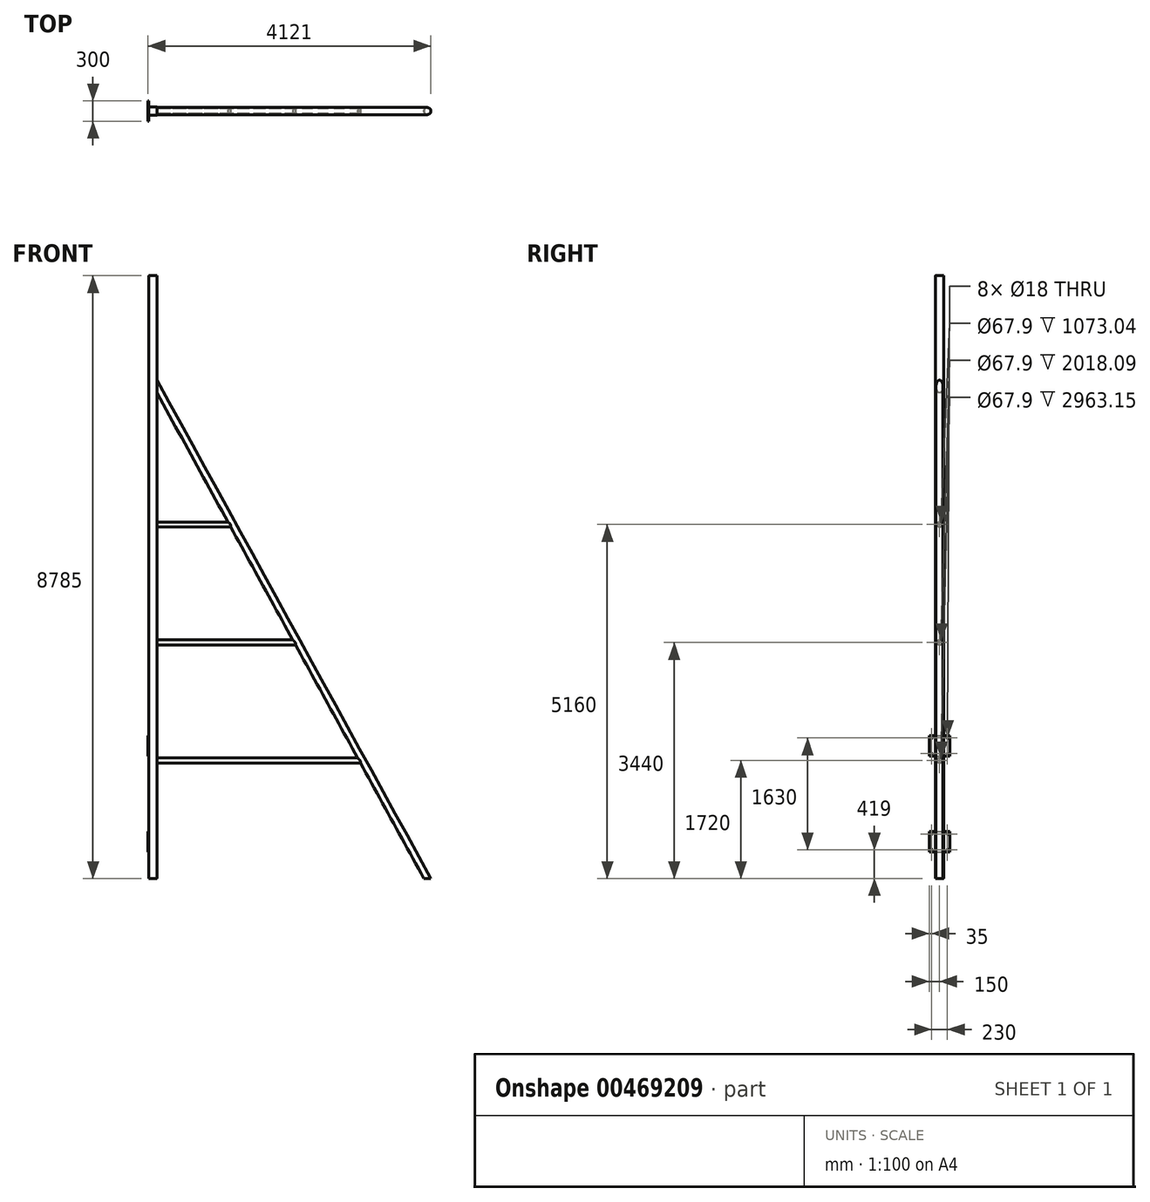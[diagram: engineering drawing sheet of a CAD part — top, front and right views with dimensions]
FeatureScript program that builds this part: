
annotation { "Feature Type Name" : "Feature", "Feature Type Description" : "" }
export const myFeature = defineFeature(function(context is Context, id is Id, definition is map)
    precondition{}
    {
        {
            var Q0;
            Q0=qCreatedBy(makeId("Top.planeOp"),FACE);
            var sketch = newSketch(context, id + "F0", { "sketchPlane" : qUnion([Q0])});
            skLineSegment(sketch, "E0.bottom", {"start": v(54, 60) * mm, "end": v(-54, 60) * mm});
            skLineSegment(sketch, "E0.top", {"start": v(54, -60) * mm, "end": v(-54, -60) * mm});
            skLineSegment(sketch, "E0.left", {"start": v(60, 54) * mm, "end": v(60, -54) * mm});
            skLineSegment(sketch, "E0.right", {"start": v(-60, 54) * mm, "end": v(-60, -54) * mm});
            skPoint(sketch, "E0.middle", {"position": v(0, 0) * mm});
            skLineSegment(sketch, "E1.0", {"start": v(51, 54) * mm, "end": v(-51, 54) * mm});
            skLineSegment(sketch, "E1.1", {"start": v(54, 51) * mm, "end": v(54, -51) * mm});
            skLineSegment(sketch, "E1.2", {"start": v(51, -54) * mm, "end": v(-51, -54) * mm});
            skLineSegment(sketch, "E1.3", {"start": v(-54, 51) * mm, "end": v(-54, -51) * mm});
            skPoint(sketch, "E2.visualSharp", {"position": v(-54, 54) * mm});
            skArc(sketch, "E2.filletArc", {"start": v(-51, 54) * mm, "mid": v(-53.12, 53.12) * mm, "end": v(-54, 51) * mm});
            skPoint(sketch, "E3.visualSharp", {"position": v(54, 54) * mm});
            skArc(sketch, "E3.filletArc", {"start": v(54, 51) * mm, "mid": v(53.12, 53.12) * mm, "end": v(51, 54) * mm});
            skPoint(sketch, "E4.visualSharp", {"position": v(54, -54) * mm});
            skArc(sketch, "E4.filletArc", {"start": v(51, -54) * mm, "mid": v(53.12, -53.12) * mm, "end": v(54, -51) * mm});
            skPoint(sketch, "E5.visualSharp", {"position": v(-54, -54) * mm});
            skArc(sketch, "E5.filletArc", {"start": v(-54, -51) * mm, "mid": v(-53.12, -53.12) * mm, "end": v(-51, -54) * mm});
            skPoint(sketch, "E6.visualSharp", {"position": v(60, -60) * mm});
            skArc(sketch, "E6.filletArc", {"start": v(54, -60) * mm, "mid": v(58.24, -58.24) * mm, "end": v(60, -54) * mm});
            skPoint(sketch, "E7.visualSharp", {"position": v(60, 60) * mm});
            skArc(sketch, "E7.filletArc", {"start": v(60, 54) * mm, "mid": v(58.24, 58.24) * mm, "end": v(54, 60) * mm});
            skPoint(sketch, "E8.visualSharp", {"position": v(-60, 60) * mm});
            skArc(sketch, "E8.filletArc", {"start": v(-54, 60) * mm, "mid": v(-58.24, 58.24) * mm, "end": v(-60, 54) * mm});
            skPoint(sketch, "E9.visualSharp", {"position": v(-60, -60) * mm});
            skArc(sketch, "E9.filletArc", {"start": v(-60, -54) * mm, "mid": v(-58.24, -58.24) * mm, "end": v(-54, -60) * mm});
            skSolve(sketch);
        }
        {
            var Q0;
            Q0=qSketchRegion(id+"F0",true);
            extrude(context, id + "F1", {"entities" : qUnion([Q0]), "depth" : 8780 * mm});
        }
        {
            var Q0;
            Q0=qCreatedBy(makeId("Top.planeOp"),FACE);
            var sketch = newSketch(context, id + "F2", { "sketchPlane" : qUnion([Q0])});
            skCircle(sketch, "E10", {"center": v(4000, 0) * mm, "radius": 48.15 * mm});
            skCircle(sketch, "E11", {"center": v(4000, 0) * mm, "radius": 51 * mm});
            skSolve(sketch);
        }
        {
            var Q0;
            Q0=qCreatedBy(makeId("Front.planeOp"),FACE);
            var sketch = newSketch(context, id + "F3", { "sketchPlane" : qUnion([Q0])});
            skLineSegment(sketch, "E12", {"start": v(4000, 0) * mm, "end": v(0, 7280) * mm});
            skSolve(sketch);
        }
        {
            var Q0;
            Q0=makeQuery(id+"F2.imprint","IMPRINT",FACE,{"disambiguationData":[TD([[makeQuery(id+"F2.imprint","IMPRINT",EDGE,{"derivedFrom":sQuery(id+"F2.wireOp",EDGE,"E10")}),-1.0]])]});
            var Q1;
            Q1=sQuery(id+"F3.wireOp",EDGE,"E12");
            sweep(context, id + "F4", {"operationType" : NewBodyOperationType.ADD, "profiles" : qUnion([Q0]), "path" : qUnion([Q1])});
        }
        {
            var Q0;
            Q0=makeQuery(id+"F1.opExtrude","CAP_FACE",FACE,{"disambiguationData":[OSD([sQuery(id+"F0.wireOp",EDGE,"E0.bottom"),sQuery(id+"F0.wireOp",EDGE,"E0.top"),sQuery(id+"F0.wireOp",EDGE,"E0.left"),sQuery(id+"F0.wireOp",EDGE,"E0.right"),sQuery(id+"F0.wireOp",EDGE,"E1.0"),sQuery(id+"F0.wireOp",EDGE,"E1.1"),sQuery(id+"F0.wireOp",EDGE,"E1.2"),sQuery(id+"F0.wireOp",EDGE,"E1.3"),sQuery(id+"F0.wireOp",EDGE,"E2.filletArc"),sQuery(id+"F0.wireOp",EDGE,"E3.filletArc"),sQuery(id+"F0.wireOp",EDGE,"E4.filletArc"),sQuery(id+"F0.wireOp",EDGE,"E5.filletArc"),sQuery(id+"F0.wireOp",EDGE,"E6.filletArc"),sQuery(id+"F0.wireOp",EDGE,"E7.filletArc"),sQuery(id+"F0.wireOp",EDGE,"E8.filletArc"),sQuery(id+"F0.wireOp",EDGE,"E9.filletArc")])],"isStart":false});
            var sketch = newSketch(context, id + "F5", { "sketchPlane" : qUnion([Q0])});
            skLineSegment(sketch, "E13.0", {"start": v(51, -54) * mm, "end": v(-51, -54) * mm});
            skArc(sketch, "E13.1", {"start": v(51, -54) * mm, "mid": v(53.12, -53.12) * mm, "end": v(54, -51) * mm});
            skLineSegment(sketch, "E13.2", {"start": v(54, 51) * mm, "end": v(54, -51) * mm});
            skArc(sketch, "E13.3", {"start": v(54, 51) * mm, "mid": v(53.12, 53.12) * mm, "end": v(51, 54) * mm});
            skLineSegment(sketch, "E13.4", {"start": v(51, 54) * mm, "end": v(-51, 54) * mm});
            skArc(sketch, "E13.5", {"start": v(-51, 54) * mm, "mid": v(-53.12, 53.12) * mm, "end": v(-54, 51) * mm});
            skLineSegment(sketch, "E13.6", {"start": v(-54, 51) * mm, "end": v(-54, -51) * mm});
            skArc(sketch, "E13.7", {"start": v(-54, -51) * mm, "mid": v(-53.12, -53.12) * mm, "end": v(-51, -54) * mm});
            skSolve(sketch);
        }
        {
            var Q0;
            Q0=qSketchRegion(id+"F5",true);
            extrude(context, id + "F6", {"entities" : qUnion([Q0]), "operationType" : NewBodyOperationType.REMOVE, "oppositeDirection" : true, "depth" : 2000 * mm});
        }
        {
            var Q0;
            Q0=makeQuery(id+"F1.opExtrude","CAP_FACE",FACE,{"disambiguationData":[OSD([sQuery(id+"F0.wireOp",EDGE,"E0.bottom"),sQuery(id+"F0.wireOp",EDGE,"E0.top"),sQuery(id+"F0.wireOp",EDGE,"E0.left"),sQuery(id+"F0.wireOp",EDGE,"E0.right"),sQuery(id+"F0.wireOp",EDGE,"E1.0"),sQuery(id+"F0.wireOp",EDGE,"E1.1"),sQuery(id+"F0.wireOp",EDGE,"E1.2"),sQuery(id+"F0.wireOp",EDGE,"E1.3"),sQuery(id+"F0.wireOp",EDGE,"E2.filletArc"),sQuery(id+"F0.wireOp",EDGE,"E3.filletArc"),sQuery(id+"F0.wireOp",EDGE,"E4.filletArc"),sQuery(id+"F0.wireOp",EDGE,"E5.filletArc"),sQuery(id+"F0.wireOp",EDGE,"E6.filletArc"),sQuery(id+"F0.wireOp",EDGE,"E7.filletArc"),sQuery(id+"F0.wireOp",EDGE,"E8.filletArc"),sQuery(id+"F0.wireOp",EDGE,"E9.filletArc")])],"isStart":false});
            var sketch = newSketch(context, id + "F7", { "sketchPlane" : qUnion([Q0])});
            skLineSegment(sketch, "E14.0", {"start": v(54, 60) * mm, "end": v(-54, 60) * mm});
            skArc(sketch, "E14.1", {"start": v(60, 54) * mm, "mid": v(58.24, 58.24) * mm, "end": v(54, 60) * mm});
            skLineSegment(sketch, "E14.2", {"start": v(60, 54) * mm, "end": v(60, -54) * mm});
            skArc(sketch, "E14.3", {"start": v(54, -60) * mm, "mid": v(58.24, -58.24) * mm, "end": v(60, -54) * mm});
            skLineSegment(sketch, "E14.4", {"start": v(54, -60) * mm, "end": v(-54, -60) * mm});
            skArc(sketch, "E14.5", {"start": v(-60, -54) * mm, "mid": v(-58.24, -58.24) * mm, "end": v(-54, -60) * mm});
            skLineSegment(sketch, "E14.6", {"start": v(-60, 54) * mm, "end": v(-60, -54) * mm});
            skArc(sketch, "E14.7", {"start": v(-54, 60) * mm, "mid": v(-58.24, 58.24) * mm, "end": v(-60, 54) * mm});
            skSolve(sketch);
        }
        {
            var Q0;
            Q0=qSketchRegion(id+"F7",true);
            extrude(context, id + "F8", {"entities" : qUnion([Q0]), "operationType" : NewBodyOperationType.ADD, "depth" : 5 * mm});
        }
        {
            var Q0;
            {var subQ1=sQuery(id+"F0.wireOp",EDGE,"E6.filletArc");var subQ13=sQuery(id+"F0.wireOp",EDGE,"E0.left");Q0=makeQuery(id+"F8.boolean.opBoolean","MERGE",FACE,{"derivedFrom":[makeQuery(id+"F4.boolean.opBoolean","SPLIT",FACE,{"disambiguationData":[TD([makeQuery(id+"F1.opExtrude","SWEPT_FACE",FACE,{"disambiguationData":[OSD([subQ1])]})])],"derivedFrom":makeQuery(id+"F1.opExtrude","SWEPT_FACE",FACE,{"disambiguationData":[OSD([subQ13])]})}),makeQuery(id+"F8.opExtrude","SWEPT_FACE",FACE,{"disambiguationData":[OSD([sQuery(id+"F7.wireOp",EDGE,"E14.2")])]})]});}
            var sketch = newSketch(context, id + "F9", { "sketchPlane" : qUnion([Q0])});
            skCircle(sketch, "E15", {"center": v(0, 1720) * mm, "radius": 36.5 * mm});
            skCircle(sketch, "E16", {"center": v(0, 1720) * mm, "radius": 33.95 * mm});
            skCircle(sketch, "E17.0.1.0", {"center": v(0, 3440) * mm, "radius": 36.5 * mm});
            skCircle(sketch, "E17.0.1.1", {"center": v(0, 3440) * mm, "radius": 33.95 * mm});
            skCircle(sketch, "E17.0.2.0", {"center": v(0, 5160) * mm, "radius": 36.5 * mm});
            skCircle(sketch, "E17.0.2.1", {"center": v(0, 5160) * mm, "radius": 33.95 * mm});
            skLineSegment(sketch, "E17.direction1", {"start": v(0, 1720) * mm, "end": v(25, 1720) * mm, "construction": true});
            skLineSegment(sketch, "E17.direction2", {"start": v(0, 1720) * mm, "end": v(0, 3440) * mm, "construction": true});
            skSolve(sketch);
        }
        {
            var Q0;
            Q0=qSketchRegion(id+"F9",true);
            extrude(context, id + "F10", {"entities" : qUnion([Q0]), "operationType" : NewBodyOperationType.ADD, "endBound" : BoundingType.UP_TO_NEXT, "depth" : 25 * mm});
        }
        {
            var Q0;
            Q0=makeQuery(id+"F8.boolean.opBoolean","MERGE",FACE,{"derivedFrom":[makeQuery(id+"F1.opExtrude","SWEPT_FACE",FACE,{"disambiguationData":[OSD([sQuery(id+"F0.wireOp",EDGE,"E0.right")])]}),makeQuery(id+"F8.opExtrude","SWEPT_FACE",FACE,{"disambiguationData":[OSD([sQuery(id+"F7.wireOp",EDGE,"E14.6")])]})]});
            var sketch = newSketch(context, id + "F11", { "sketchPlane" : qUnion([Q0])});
            skLineSegment(sketch, "E18.bottom", {"start": v(150, 684) * mm, "end": v(-150, 684) * mm});
            skLineSegment(sketch, "E18.top", {"start": v(150, 384) * mm, "end": v(-150, 384) * mm});
            skLineSegment(sketch, "E18.left", {"start": v(150, 684) * mm, "end": v(150, 384) * mm});
            skLineSegment(sketch, "E18.right", {"start": v(-150, 684) * mm, "end": v(-150, 384) * mm});
            skPoint(sketch, "E18.middle", {"position": v(0, 534) * mm});
            skLineSegment(sketch, "E19.direction1", {"start": v(-150, 384) * mm, "end": v(-125, 384) * mm, "construction": true});
            skCircle(sketch, "E20", {"center": v(-115, 649) * mm, "radius": 9 * mm});
            skCircle(sketch, "E21", {"center": v(115, 649) * mm, "radius": 9 * mm});
            skCircle(sketch, "E22", {"center": v(115, 419) * mm, "radius": 9 * mm});
            skCircle(sketch, "E23", {"center": v(-115, 419) * mm, "radius": 9 * mm});
            skLineSegment(sketch, "E24.0.1.0", {"start": v(-150, 2084) * mm, "end": v(-150, 1784) * mm});
            skLineSegment(sketch, "E24.0.1.1", {"start": v(150, 2084) * mm, "end": v(150, 1784) * mm});
            skPoint(sketch, "E24.0.1.2", {"position": v(0, 1934) * mm});
            skLineSegment(sketch, "E24.0.1.3", {"start": v(150, 1784) * mm, "end": v(-150, 1784) * mm});
            skLineSegment(sketch, "E24.0.1.4", {"start": v(150, 2084) * mm, "end": v(-150, 2084) * mm});
            skCircle(sketch, "E24.0.1.5", {"center": v(-115, 2049) * mm, "radius": 9 * mm});
            skCircle(sketch, "E24.0.1.6", {"center": v(115, 2049) * mm, "radius": 9 * mm});
            skCircle(sketch, "E24.0.1.7", {"center": v(115, 1819) * mm, "radius": 9 * mm});
            skLineSegment(sketch, "E24.0.1.8", {"start": v(-150, 1784) * mm, "end": v(-125, 1784) * mm, "construction": true});
            skCircle(sketch, "E24.0.1.9", {"center": v(-115, 1819) * mm, "radius": 9 * mm});
            skLineSegment(sketch, "E24.direction1", {"start": v(-150, 384) * mm, "end": v(-137.5, 384) * mm, "construction": true});
            skLineSegment(sketch, "E24.direction2", {"start": v(-150, 384) * mm, "end": v(-150, 1784) * mm, "construction": true});
            skSolve(sketch);
        }
        {
            var Q0;
            Q0=qSketchRegion(id+"F11",true);
            extrude(context, id + "F12", {"entities" : qUnion([Q0]), "operationType" : NewBodyOperationType.ADD, "depth" : 10 * mm});
        }
    });
